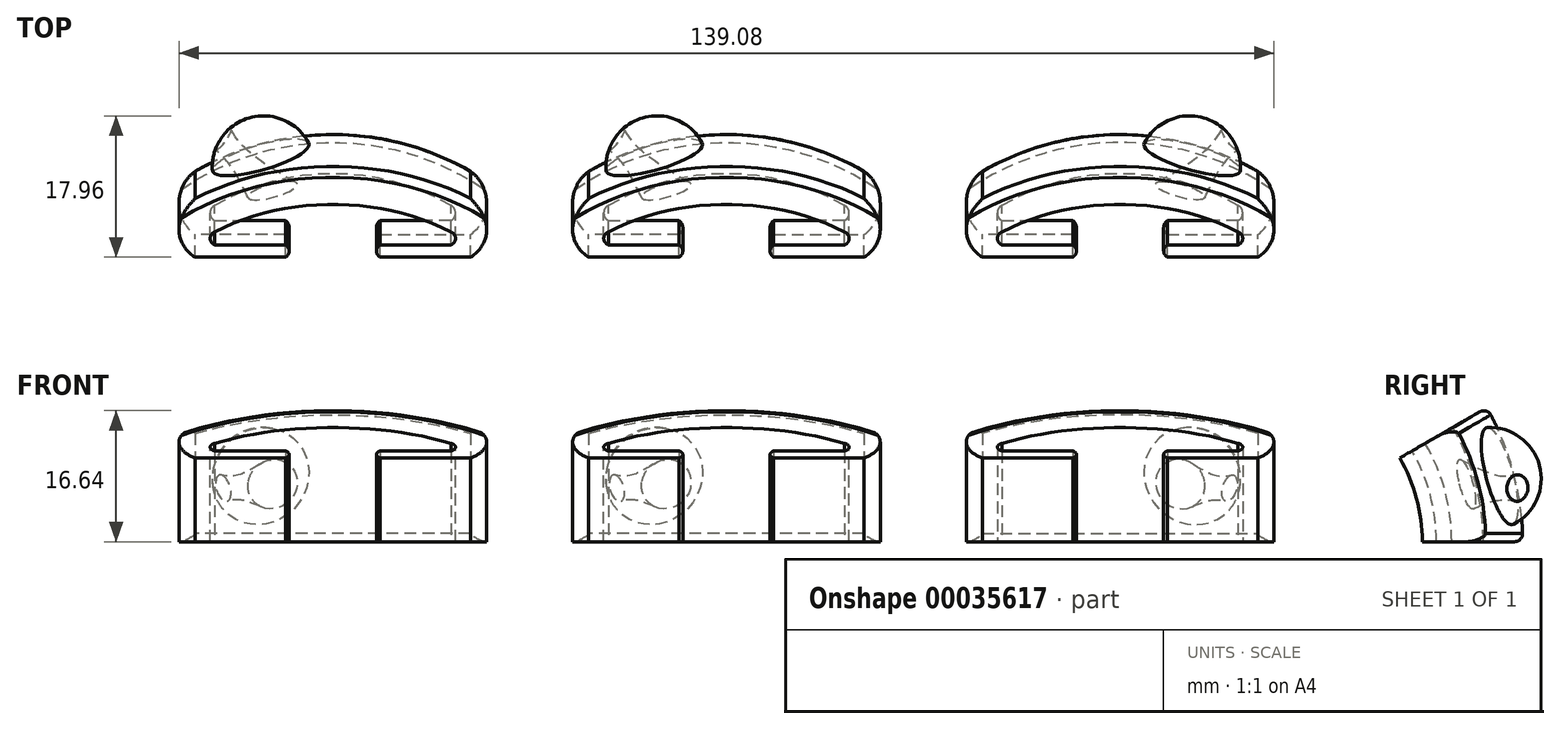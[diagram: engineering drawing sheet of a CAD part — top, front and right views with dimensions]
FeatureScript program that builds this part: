
annotation { "Feature Type Name" : "Feature", "Feature Type Description" : "" }
export const myFeature = defineFeature(function(context is Context, id is Id, definition is map)
    precondition{}
    {
        {
            var Q0;
            Q0=qCreatedBy(makeId("Top.planeOp"),FACE);
            var sketch = newSketch(context, id + "F0", { "sketchPlane" : qUnion([Q0])});
            skLineSegment(sketch, "E0", {"start": v(-15, 0) * mm, "end": v(15, 0) * mm, "construction": true});
            skArc(sketch, "E1", {"start": v(15, 0) * mm, "mid": v(0, 4.02) * mm, "end": v(-15, 0) * mm});
            skArc(sketch, "E2.0", {"start": v(17.5, 4.33) * mm, "mid": v(0, 9.02) * mm, "end": v(-17.5, 4.33) * mm});
            skArc(sketch, "E3", {"start": v(-15, 0) * mm, "mid": v(-15.58, -0.97) * mm, "end": v(-15, -1.94) * mm});
            skLineSegment(sketch, "E4", {"start": v(0, 0) * mm, "end": v(0, -25) * mm, "construction": true});
            skArc(sketch, "E5.MirrorCS", {"start": v(15, 0) * mm, "mid": v(15.58, -0.97) * mm, "end": v(15, -1.94) * mm});
            skLineSegment(sketch, "E6", {"start": v(-15, -1.94) * mm, "end": v(-6, -1.94) * mm});
            skArc(sketch, "E7", {"start": v(-6, -3.73) * mm, "mid": v(-5.54, -2.83) * mm, "end": v(-6, -1.94) * mm});
            skLineSegment(sketch, "E8", {"start": v(-6, -3.73) * mm, "end": v(-17.5, -3.73) * mm});
            skArc(sketch, "E9", {"start": v(-17.5, 4.33) * mm, "mid": v(-19.54, 0.3) * mm, "end": v(-17.5, -3.73) * mm});
            skLineSegment(sketch, "E10.MirrorCS", {"start": v(15, -1.94) * mm, "end": v(6, -1.94) * mm});
            skArc(sketch, "E11.MirrorCS", {"start": v(6, -3.73) * mm, "mid": v(5.54, -2.83) * mm, "end": v(6, -1.94) * mm});
            skLineSegment(sketch, "E12.MirrorCS", {"start": v(6, -3.73) * mm, "end": v(17.5, -3.73) * mm});
            skArc(sketch, "E13.MirrorCS", {"start": v(17.5, 4.33) * mm, "mid": v(19.54, 0.3) * mm, "end": v(17.5, -3.73) * mm});
            skLineSegment(sketch, "E14", {"start": v(-5, -25) * mm, "end": v(5, -25) * mm, "construction": true});
            skSolve(sketch);
        }
        {
            var Q0;
            Q0 = qSketchRegion(id + "F0", true);
            var Q1;
            Q1=sQuery(id+"F0.wireOp",EDGE,"E14");
            revolve(context, id + "F1", {"entities" : qUnion([Q0]), "axis" : qUnion([Q1]), "revolveType" : RevolveType.ONE_DIRECTION, "angle" : 30 * degree});
        }
        {
            var Q0;
            Q0=makeQuery(id+"F1.opRevolve","CAP_EDGE",EDGE,{"disambiguationData":[OSD([sQuery(id+"F0.wireOp",EDGE,"E2.0")])],"isStart":false});
            var Q1;
            Q1=makeQuery(id+"F1.opRevolve","CAP_EDGE",EDGE,{"disambiguationData":[OSD([sQuery(id+"F0.wireOp",EDGE,"E2.0")])],"isStart":true});
            fillet(context, id + "F2", {"entities" : qUnion([Q0, Q1]), "radius" : 1 * mm, "tangentPropagation" : true, "allowEdgeOverflow" : false});
        }
        {
            var Q0;
            Q0=qCreatedBy(makeId("Top.planeOp"),FACE);
            var sketch = newSketch(context, id + "F3", { "sketchPlane" : qUnion([Q0])});
            skLineSegment(sketch, "E15", {"start": v(0, 0) * mm, "end": v(0, 9.5) * mm, "construction": true});
            skSolve(sketch);
        }
        {
            var Q0;
            {var subQ0=sQuery(id+"F0.wireOp",EDGE,"E2.0");Q0=makeQuery(id+"F2.opFillet","BLEND_VERTEX",VERTEX,{"blendedFrom":[makeQuery(id+"F1.opRevolve","CAP_EDGE",EDGE,{"disambiguationData":[OSD([subQ0])],"isStart":false}),makeQuery(id+"F1.opRevolve","SWEPT_FACE",FACE,{"disambiguationData":[OSD([subQ0])]}),makeQuery(id+"F1.opRevolve","SWEPT_FACE",FACE,{"disambiguationData":[OSD([sQuery(id+"F0.wireOp",EDGE,"E9")])]})],"blendedInto":[makeQuery(id+"F1.opRevolve","SWEPT_FACE",FACE,{"disambiguationData":[OSD([subQ0])]}),makeQuery(id+"F1.opRevolve","SWEPT_FACE",FACE,{"disambiguationData":[OSD([sQuery(id+"F0.wireOp",EDGE,"E9")])]})]});}
            var Q1;
            {var subQ0=sQuery(id+"F0.wireOp",EDGE,"E2.0");Q1=makeQuery(id+"F2.opFillet","BLEND_VERTEX",VERTEX,{"blendedFrom":[makeQuery(id+"F1.opRevolve","CAP_EDGE",EDGE,{"disambiguationData":[OSD([subQ0])],"isStart":true}),makeQuery(id+"F1.opRevolve","SWEPT_FACE",FACE,{"disambiguationData":[OSD([subQ0])]}),makeQuery(id+"F1.opRevolve","SWEPT_FACE",FACE,{"disambiguationData":[OSD([sQuery(id+"F0.wireOp",EDGE,"E9")])]})],"blendedInto":[makeQuery(id+"F1.opRevolve","SWEPT_FACE",FACE,{"disambiguationData":[OSD([subQ0])]}),makeQuery(id+"F1.opRevolve","SWEPT_FACE",FACE,{"disambiguationData":[OSD([sQuery(id+"F0.wireOp",EDGE,"E9")])]})]});}
            var Q2;
            Q2=sQuery(id+"F3.wireOp",VERTEX,"E15.end");
            cPlane(context, id + "F4", {"entities" : qUnion([Q0, Q1, Q2]), "cplaneType" : CPlaneType.THREE_POINT, "offset" : 150 * mm, "width" : 150 * mm, "height" : 150 * mm});
        }
        {
            var Q0;
            Q0=qCreatedBy(id+"F4.planeOp",FACE);
            var sketch = newSketch(context, id + "F5", { "sketchPlane" : qUnion([Q0])});
            skPoint(sketch, "E16.0", {"position": v(15.73, 13.06) * mm});
            skPoint(sketch, "E17.0", {"position": v(15.73, -0.12) * mm});
            skLineSegment(sketch, "E18", {"start": v(15.73, 13.06) * mm, "end": v(15.73, -0.12) * mm, "construction": true});
            skLineSegment(sketch, "E19", {"start": v(15.73, 6.47) * mm, "end": v(6.73, 6.47) * mm, "construction": true});
            skLineSegment(sketch, "E20", {"start": v(6.73, 12.97) * mm, "end": v(6.73, -0.03) * mm});
            skArc(sketch, "E21", {"start": v(6.73, 12.97) * mm, "mid": v(0.23, 6.47) * mm, "end": v(6.73, -0.03) * mm});
            skSolve(sketch);
        }
        {
            var Q0;
            Q0 = qSketchRegion(id + "F5", true);
            var Q1;
            Q1=sQuery(id+"F5.wireOp",EDGE,"E20");
            revolve(context, id + "F6", {"operationType" : NewBodyOperationType.ADD, "entities" : qUnion([Q0]), "axis" : qUnion([Q1]), "revolveType" : RevolveType.ONE_DIRECTION, "oppositeDirection" : true, "angle" : 180 * degree});
        }
        {
            var Q0;
            Q0=qCreatedBy(id+"F4.planeOp",FACE);
            cPlane(context, id + "F7", {"entities" : qUnion([Q0]), "cplaneType" : CPlaneType.OFFSET, "offset" : 10 * mm, "width" : 150 * mm, "height" : 150 * mm});
        }
        {
            var Q0;
            Q0=qCreatedBy(id+"F4.planeOp",FACE);
            cPlane(context, id + "F8", {"entities" : qUnion([Q0]), "cplaneType" : CPlaneType.OFFSET, "offset" : 5 * mm, "oppositeDirection" : true, "width" : 150 * mm, "height" : 150 * mm});
        }
        {
            var Q0;
            Q0=qCreatedBy(id+"F8.planeOp",FACE);
            var sketch = newSketch(context, id + "F9", { "sketchPlane" : qUnion([Q0])});
            skLineSegment(sketch, "E22", {"start": v(5.35, 7.09) * mm, "end": v(1.35, 7.09) * mm, "construction": true});
            skCircle(sketch, "E23", {"center": v(5.35, 7.09) * mm, "radius": 4 * mm});
            skSolve(sketch);
        }
        {
            var Q0;
            Q0=qCreatedBy(id+"F7.planeOp",FACE);
            var sketch = newSketch(context, id + "F10", { "sketchPlane" : qUnion([Q0])});
            skLineSegment(sketch, "E24", {"start": v(14.66, 2.57) * mm, "end": v(10.66, 2.57) * mm, "construction": true});
            skCircle(sketch, "E25", {"center": v(14.66, 2.57) * mm, "radius": 4 * mm});
            skSolve(sketch);
        }
        {
            var Q1;
            Q1=makeQuery(id+"F9.imprint","IMPRINT",FACE,{"disambiguationData":[TD([[makeQuery(id+"F9.imprint","IMPRINT",EDGE,{"derivedFrom":sQuery(id+"F9.wireOp",EDGE,"E23")}),1.0]])]});
            var Q2;
            Q2=makeQuery(id+"F10.imprint","IMPRINT",FACE,{"disambiguationData":[TD([[makeQuery(id+"F10.imprint","IMPRINT",EDGE,{"derivedFrom":sQuery(id+"F10.wireOp",EDGE,"E25")}),1.0]])]});
            loft(context, id + "F11", {"operationType" : NewBodyOperationType.REMOVE, "sheetProfilesArray" : [{ "sheetProfileEntities" : qUnion([Q1]) }, { "sheetProfileEntities" : qUnion([Q2]) }]});
        }
        {
            var Q0;
            Q0=makeQuery(id+"F1.opRevolve","SWEPT_BODY",BODY,{"disambiguationData":[OSD([sQuery(id+"F0.wireOp",EDGE,"E1"),sQuery(id+"F0.wireOp",EDGE,"E2.0"),sQuery(id+"F0.wireOp",EDGE,"E3"),sQuery(id+"F0.wireOp",EDGE,"E5.MirrorCS"),sQuery(id+"F0.wireOp",EDGE,"E6"),sQuery(id+"F0.wireOp",EDGE,"E7"),sQuery(id+"F0.wireOp",EDGE,"E8"),sQuery(id+"F0.wireOp",EDGE,"E9"),sQuery(id+"F0.wireOp",EDGE,"E10.MirrorCS"),sQuery(id+"F0.wireOp",EDGE,"E11.MirrorCS"),sQuery(id+"F0.wireOp",EDGE,"E12.MirrorCS"),sQuery(id+"F0.wireOp",EDGE,"E13.MirrorCS")])]});
            transform(context, id + "F12", {"entities" : qUnion([Q0]), "transformType" : TransformType.TRANSLATION_3D, "dx" : -50 * mm, "dy" : 0 * mm, "dz" : 0 * mm, "makeCopy" : true});
        }
        {
            var Q0;
            Q0=makeQuery(id+"F12.opPattern","COPY",BODY,{"derivedFrom":makeQuery(id+"F1.opRevolve","SWEPT_BODY",BODY,{"disambiguationData":[OSD([sQuery(id+"F0.wireOp",EDGE,"E1"),sQuery(id+"F0.wireOp",EDGE,"E2.0"),sQuery(id+"F0.wireOp",EDGE,"E3"),sQuery(id+"F0.wireOp",EDGE,"E5.MirrorCS"),sQuery(id+"F0.wireOp",EDGE,"E6"),sQuery(id+"F0.wireOp",EDGE,"E7"),sQuery(id+"F0.wireOp",EDGE,"E8"),sQuery(id+"F0.wireOp",EDGE,"E9"),sQuery(id+"F0.wireOp",EDGE,"E10.MirrorCS"),sQuery(id+"F0.wireOp",EDGE,"E11.MirrorCS"),sQuery(id+"F0.wireOp",EDGE,"E12.MirrorCS"),sQuery(id+"F0.wireOp",EDGE,"E13.MirrorCS")])]}),"instanceName":"1"});
            var Q1;
            Q1=makeQuery(id+"F12.opPattern","COPY",FACE,{"derivedFrom":makeQuery(id+"F6.opRevolve","SWEPT_FACE",FACE,{"disambiguationData":[OSD([sQuery(id+"F5.wireOp",EDGE,"E21")])]}),"instanceName":"1"});
            var Q2;
            Q2=makeQuery(id+"F12.opPattern","COPY",FACE,{"derivedFrom":makeQuery(id+"F11.boolean.opBoolean","COPY",FACE,{"derivedFrom":makeQuery(id+"F11.opLoft","SWEPT_FACE",FACE,{"disambiguationData":[OSD([sQuery(id+"F9.wireOp",EDGE,"E23"),sQuery(id+"F10.wireOp",EDGE,"E25")])]})}),"instanceName":"1"});
            var Q3;
            Q3=makeQuery(id+"F12.opPattern","COPY",FACE,{"derivedFrom":makeQuery(id+"F1.opRevolve","SWEPT_FACE",FACE,{"disambiguationData":[OSD([sQuery(id+"F0.wireOp",EDGE,"E13.MirrorCS")])]}),"instanceName":"1"});
            var Q4;
            Q4=makeQuery(id+"F12.opPattern","COPY",FACE,{"derivedFrom":makeQuery(id+"F1.opRevolve","SWEPT_FACE",FACE,{"disambiguationData":[OSD([sQuery(id+"F0.wireOp",EDGE,"E2.0")])]}),"instanceName":"1"});
            var Q5;
            Q5=makeQuery(id+"F12.opPattern","COPY",FACE,{"derivedFrom":makeQuery(id+"F1.opRevolve","SWEPT_FACE",FACE,{"disambiguationData":[OSD([sQuery(id+"F0.wireOp",EDGE,"E1")])]}),"instanceName":"1"});
            var Q6;
            Q6=makeQuery(id+"F12.opPattern","COPY",FACE,{"derivedFrom":makeQuery(id+"F1.opRevolve","SWEPT_FACE",FACE,{"disambiguationData":[OSD([sQuery(id+"F0.wireOp",EDGE,"E6")])]}),"instanceName":"1"});
            var Q7;
            Q7=makeQuery(id+"F12.opPattern","COPY",FACE,{"derivedFrom":makeQuery(id+"F1.opRevolve","SWEPT_FACE",FACE,{"disambiguationData":[OSD([sQuery(id+"F0.wireOp",EDGE,"E7")])]}),"instanceName":"1"});
            var Q8;
            Q8=makeQuery(id+"F12.opPattern","COPY",FACE,{"derivedFrom":makeQuery(id+"F1.opRevolve","SWEPT_FACE",FACE,{"disambiguationData":[OSD([sQuery(id+"F0.wireOp",EDGE,"E10.MirrorCS")])]}),"instanceName":"1"});
            var Q9;
            Q9=makeQuery(id+"F12.opPattern","COPY",FACE,{"derivedFrom":makeQuery(id+"F1.opRevolve","SWEPT_FACE",FACE,{"disambiguationData":[OSD([sQuery(id+"F0.wireOp",EDGE,"E11.MirrorCS")])]}),"instanceName":"1"});
            var Q10;
            {var subQ0=sQuery(id+"F0.wireOp",EDGE,"E2.0");Q10=makeQuery(id+"F12.opPattern","COPY",FACE,{"derivedFrom":makeQuery(id+"F2.opFillet","BLEND_FACE",FACE,{"disambiguationData":[OSD([subQ0]),TDD([makeQuery(id+"F1.opRevolve","CAP_EDGE",EDGE,{"disambiguationData":[OSD([subQ0])],"isStart":true})])]}),"instanceName":"1"});}
            var Q11;
            {var subQ0=sQuery(id+"F0.wireOp",EDGE,"E2.0");Q11=makeQuery(id+"F12.opPattern","COPY",FACE,{"derivedFrom":makeQuery(id+"F2.opFillet","BLEND_FACE",FACE,{"disambiguationData":[OSD([subQ0]),TDD([makeQuery(id+"F1.opRevolve","CAP_EDGE",EDGE,{"disambiguationData":[OSD([subQ0])],"isStart":false})])]}),"instanceName":"1"});}
            var Q12;
            Q12=makeQuery(id+"F12.opPattern","COPY",FACE,{"derivedFrom":makeQuery(id+"F1.opRevolve","CAP_FACE",FACE,{"disambiguationData":[OSD([sQuery(id+"F0.wireOp",EDGE,"E1"),sQuery(id+"F0.wireOp",EDGE,"E2.0"),sQuery(id+"F0.wireOp",EDGE,"E3"),sQuery(id+"F0.wireOp",EDGE,"E5.MirrorCS"),sQuery(id+"F0.wireOp",EDGE,"E6"),sQuery(id+"F0.wireOp",EDGE,"E7"),sQuery(id+"F0.wireOp",EDGE,"E8"),sQuery(id+"F0.wireOp",EDGE,"E9"),sQuery(id+"F0.wireOp",EDGE,"E10.MirrorCS"),sQuery(id+"F0.wireOp",EDGE,"E11.MirrorCS"),sQuery(id+"F0.wireOp",EDGE,"E12.MirrorCS"),sQuery(id+"F0.wireOp",EDGE,"E13.MirrorCS")])],"isStart":false}),"instanceName":"1"});
            var Q13;
            Q13=makeQuery(id+"F12.opPattern","COPY",FACE,{"derivedFrom":makeQuery(id+"F1.opRevolve","SWEPT_FACE",FACE,{"disambiguationData":[OSD([sQuery(id+"F0.wireOp",EDGE,"E9")])]}),"instanceName":"1"});
            var Q14;
            Q14=makeQuery(id+"F12.opPattern","COPY",FACE,{"derivedFrom":makeQuery(id+"F1.opRevolve","SWEPT_FACE",FACE,{"disambiguationData":[OSD([sQuery(id+"F0.wireOp",EDGE,"E3")])]}),"instanceName":"1"});
            var Q15;
            Q15=makeQuery(id+"F12.opPattern","COPY",FACE,{"derivedFrom":makeQuery(id+"F1.opRevolve","SWEPT_FACE",FACE,{"disambiguationData":[OSD([sQuery(id+"F0.wireOp",EDGE,"E5.MirrorCS")])]}),"instanceName":"1"});
            var Q16;
            Q16=makeQuery(id+"F12.opPattern","COPY",FACE,{"derivedFrom":makeQuery(id+"F1.opRevolve","SWEPT_FACE",FACE,{"disambiguationData":[OSD([sQuery(id+"F0.wireOp",EDGE,"E8")])]}),"instanceName":"1"});
            var Q17;
            Q17=makeQuery(id+"F12.opPattern","COPY",FACE,{"derivedFrom":makeQuery(id+"F1.opRevolve","SWEPT_FACE",FACE,{"disambiguationData":[OSD([sQuery(id+"F0.wireOp",EDGE,"E12.MirrorCS")])]}),"instanceName":"1"});
            var Q18;
            Q18=makeQuery(id+"F12.opPattern","COPY",FACE,{"derivedFrom":makeQuery(id+"F1.opRevolve","CAP_FACE",FACE,{"disambiguationData":[OSD([sQuery(id+"F0.wireOp",EDGE,"E1"),sQuery(id+"F0.wireOp",EDGE,"E2.0"),sQuery(id+"F0.wireOp",EDGE,"E3"),sQuery(id+"F0.wireOp",EDGE,"E5.MirrorCS"),sQuery(id+"F0.wireOp",EDGE,"E6"),sQuery(id+"F0.wireOp",EDGE,"E7"),sQuery(id+"F0.wireOp",EDGE,"E8"),sQuery(id+"F0.wireOp",EDGE,"E9"),sQuery(id+"F0.wireOp",EDGE,"E10.MirrorCS"),sQuery(id+"F0.wireOp",EDGE,"E11.MirrorCS"),sQuery(id+"F0.wireOp",EDGE,"E12.MirrorCS"),sQuery(id+"F0.wireOp",EDGE,"E13.MirrorCS")])],"isStart":true}),"instanceName":"1"});
            var Q19;
            Q19=qCreatedBy(makeId("Right.planeOp"),FACE);
            mirror(context, id + "F13", {"entities" : qUnion([Q0]), "faces" : qUnion([Q1, Q2, Q3, Q4, Q5, Q6, Q7, Q8, Q9, Q10, Q11, Q12, Q13, Q14, Q15, Q16, Q17, Q18]), "mirrorPlane" : qUnion([Q19]), "patternType" : MirrorType.FACE});
        }
    });
